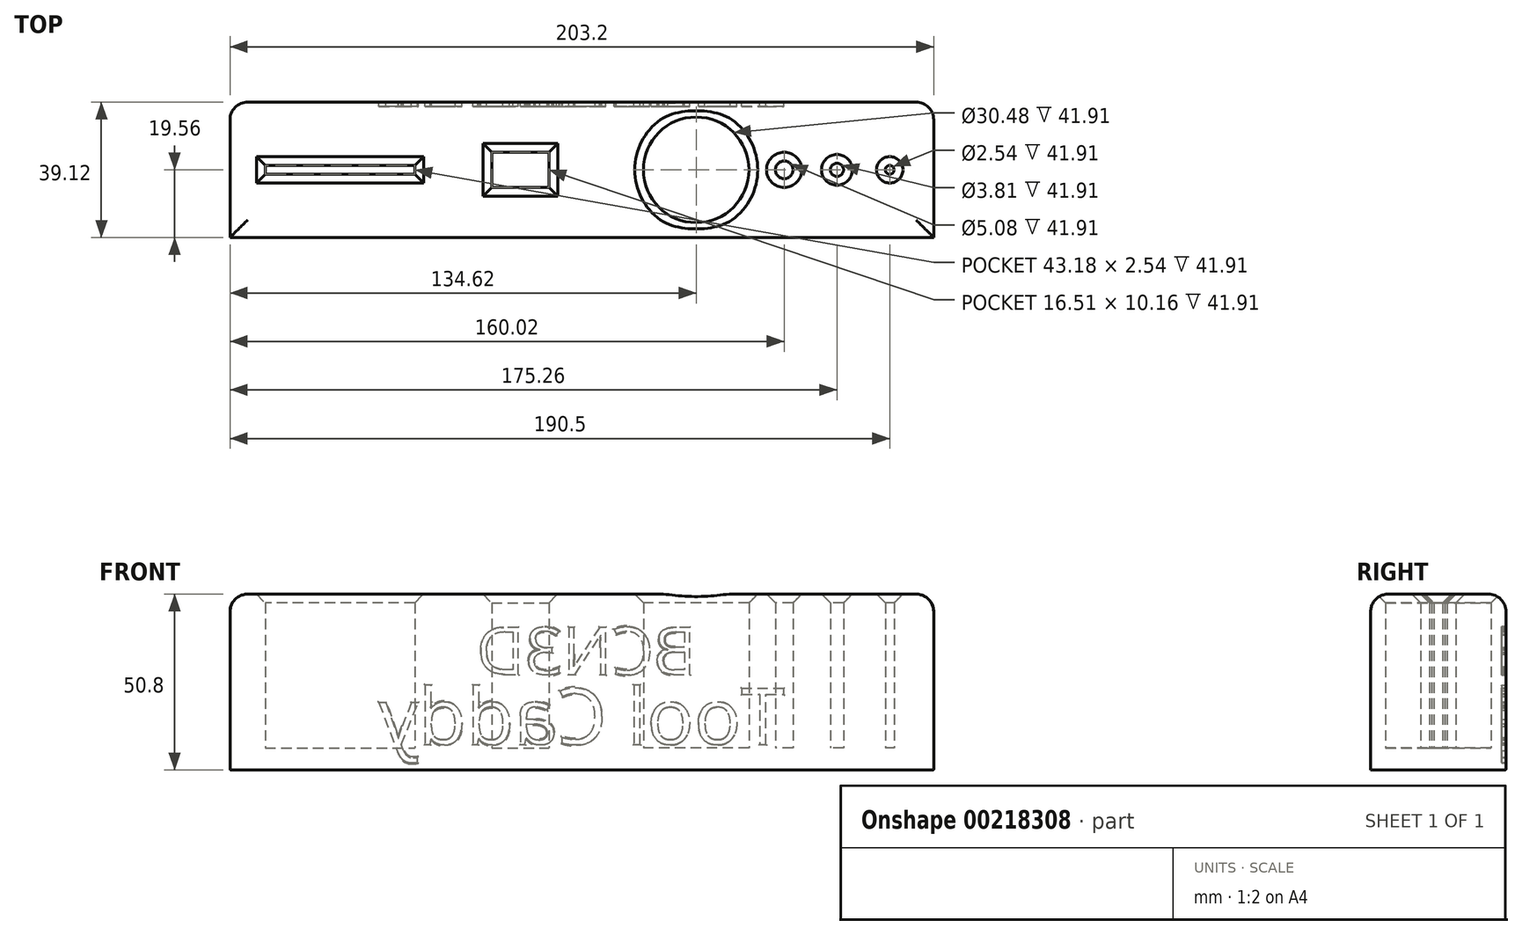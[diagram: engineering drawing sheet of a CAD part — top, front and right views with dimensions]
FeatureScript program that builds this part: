
annotation { "Feature Type Name" : "Feature", "Feature Type Description" : "" }
export const myFeature = defineFeature(function(context is Context, id is Id, definition is map)
    precondition{}
    {
        {
            var Q0;
            Q0=qCreatedBy(makeId("Top.planeOp"),FACE);
            var sketch = newSketch(context, id + "F0", { "sketchPlane" : qUnion([Q0])});
            skLineSegment(sketch, "E0.bottom", {"start": v(101.6, 19.56) * mm, "end": v(-101.6, 19.56) * mm});
            skLineSegment(sketch, "E0.top", {"start": v(101.6, -19.56) * mm, "end": v(-101.6, -19.56) * mm});
            skLineSegment(sketch, "E0.left", {"start": v(101.6, 19.56) * mm, "end": v(101.6, -19.56) * mm});
            skLineSegment(sketch, "E0.right", {"start": v(-101.6, 19.56) * mm, "end": v(-101.6, -19.56) * mm});
            skPoint(sketch, "E0.middle", {"position": v(0, 0) * mm});
            skLineSegment(sketch, "E1.bottom", {"start": v(-91.44, 1.27) * mm, "end": v(-48.26, 1.27) * mm});
            skLineSegment(sketch, "E1.top", {"start": v(-91.44, -1.27) * mm, "end": v(-48.26, -1.27) * mm});
            skLineSegment(sketch, "E1.left", {"start": v(-91.44, 1.27) * mm, "end": v(-91.44, -1.27) * mm});
            skLineSegment(sketch, "E1.right", {"start": v(-48.26, 1.27) * mm, "end": v(-48.26, -1.27) * mm});
            skPoint(sketch, "E1.middle", {"position": v(-69.85, 0) * mm});
            skLineSegment(sketch, "E2.bottom", {"start": v(-26.04, -5.08) * mm, "end": v(-9.53, -5.08) * mm});
            skLineSegment(sketch, "E2.top", {"start": v(-26.04, 5.08) * mm, "end": v(-9.53, 5.08) * mm});
            skLineSegment(sketch, "E2.left", {"start": v(-26.04, -5.08) * mm, "end": v(-26.04, 5.08) * mm});
            skLineSegment(sketch, "E2.right", {"start": v(-9.53, -5.08) * mm, "end": v(-9.53, 5.08) * mm});
            skPoint(sketch, "E2.middle", {"position": v(-17.78, 0) * mm});
            skCircle(sketch, "E3", {"center": v(58.42, 0) * mm, "radius": 2.54 * mm});
            skCircle(sketch, "E4", {"center": v(73.66, 0) * mm, "radius": 1.9 * mm});
            skCircle(sketch, "E5", {"center": v(88.9, 0) * mm, "radius": 1.27 * mm});
            skCircle(sketch, "E6", {"center": v(33.02, 0) * mm, "radius": 15.24 * mm});
            skSolve(sketch);
        }
        {
            var Q0;
            Q0=qSketchRegion(id+"F0",true);
            extrude(context, id + "F1", {"entities" : qUnion([Q0]), "depth" : 50.8 * mm});
        }
        {
            var Q0;
            Q0=makeQuery(id+"F0.imprint","IMPRINT",FACE,{"disambiguationData":[TD([[makeQuery(id+"F0.imprint","IMPRINT",EDGE,{"derivedFrom":sQuery(id+"F0.wireOp",EDGE,"E1.bottom")}),-1.0]])]});
            var Q1;
            Q1=makeQuery(id+"F0.imprint","IMPRINT",FACE,{"disambiguationData":[TD([[makeQuery(id+"F0.imprint","IMPRINT",EDGE,{"derivedFrom":sQuery(id+"F0.wireOp",EDGE,"E2.bottom")}),1.0]])]});
            var Q2;
            Q2=makeQuery(id+"F0.imprint","IMPRINT",FACE,{"disambiguationData":[TD([[makeQuery(id+"F0.imprint","IMPRINT",EDGE,{"derivedFrom":sQuery(id+"F0.wireOp",EDGE,"E3")}),1.0]])]});
            var Q3;
            Q3=makeQuery(id+"F0.imprint","IMPRINT",FACE,{"disambiguationData":[TD([[makeQuery(id+"F0.imprint","IMPRINT",EDGE,{"derivedFrom":sQuery(id+"F0.wireOp",EDGE,"E4")}),1.0]])]});
            var Q4;
            Q4=makeQuery(id+"F0.imprint","IMPRINT",FACE,{"disambiguationData":[TD([[makeQuery(id+"F0.imprint","IMPRINT",EDGE,{"derivedFrom":sQuery(id+"F0.wireOp",EDGE,"E5")}),1.0]])]});
            var Q5;
            Q5=makeQuery(id+"F0.imprint","IMPRINT",FACE,{"disambiguationData":[TD([[makeQuery(id+"F0.imprint","IMPRINT",EDGE,{"derivedFrom":sQuery(id+"F0.wireOp",EDGE,"E6")}),1.0]])]});
            extrude(context, id + "F2", {"entities" : qUnion([Q0, Q1, Q2, Q3, Q4, Q5]), "operationType" : NewBodyOperationType.ADD, "depth" : 6.35 * mm});
        }
        {
            var Q0;
            Q0=makeQuery(id+"F1.opExtrude","CAP_EDGE",EDGE,{"disambiguationData":[OSD([sQuery(id+"F0.wireOp",EDGE,"E1.bottom")])],"isStart":false});
            var Q1;
            Q1=makeQuery(id+"F1.opExtrude","CAP_EDGE",EDGE,{"disambiguationData":[OSD([sQuery(id+"F0.wireOp",EDGE,"E1.top")])],"isStart":false});
            var Q2;
            Q2=makeQuery(id+"F1.opExtrude","CAP_EDGE",EDGE,{"disambiguationData":[OSD([sQuery(id+"F0.wireOp",EDGE,"E1.left")])],"isStart":false});
            var Q3;
            Q3=makeQuery(id+"F1.opExtrude","CAP_EDGE",EDGE,{"disambiguationData":[OSD([sQuery(id+"F0.wireOp",EDGE,"E1.right")])],"isStart":false});
            var Q4;
            Q4=makeQuery(id+"F1.opExtrude","CAP_EDGE",EDGE,{"disambiguationData":[OSD([sQuery(id+"F0.wireOp",EDGE,"E2.bottom")])],"isStart":false});
            var Q5;
            Q5=makeQuery(id+"F1.opExtrude","CAP_EDGE",EDGE,{"disambiguationData":[OSD([sQuery(id+"F0.wireOp",EDGE,"E2.left")])],"isStart":false});
            var Q6;
            Q6=makeQuery(id+"F1.opExtrude","CAP_EDGE",EDGE,{"disambiguationData":[OSD([sQuery(id+"F0.wireOp",EDGE,"E2.top")])],"isStart":false});
            var Q7;
            Q7=makeQuery(id+"F1.opExtrude","CAP_EDGE",EDGE,{"disambiguationData":[OSD([sQuery(id+"F0.wireOp",EDGE,"E2.right")])],"isStart":false});
            var Q8;
            Q8=makeQuery(id+"F1.opExtrude","CAP_EDGE",EDGE,{"disambiguationData":[OSD([sQuery(id+"F0.wireOp",EDGE,"E3")])],"isStart":false});
            var Q9;
            Q9=makeQuery(id+"F1.opExtrude","CAP_EDGE",EDGE,{"disambiguationData":[OSD([sQuery(id+"F0.wireOp",EDGE,"E4")])],"isStart":false});
            var Q10;
            Q10=makeQuery(id+"F1.opExtrude","CAP_EDGE",EDGE,{"disambiguationData":[OSD([sQuery(id+"F0.wireOp",EDGE,"E5")])],"isStart":false});
            var Q11;
            Q11=makeQuery(id+"F1.opExtrude","CAP_EDGE",EDGE,{"disambiguationData":[OSD([sQuery(id+"F0.wireOp",EDGE,"E6")])],"isStart":false});
            chamfer(context, id + "F3", {"entities" : qUnion([Q0, Q1, Q2, Q3, Q4, Q5, Q6, Q7, Q8, Q9, Q10, Q11]), "width" : 2.54 * mm, "tangentPropagation" : true});
        }
        {
            var Q0;
            Q0=makeQuery(id+"F1.opExtrude","CAP_EDGE",EDGE,{"disambiguationData":[OSD([sQuery(id+"F0.wireOp",EDGE,"E0.right")])],"isStart":false});
            var Q1;
            Q1=makeQuery(id+"F1.opExtrude","CAP_EDGE",EDGE,{"disambiguationData":[OSD([sQuery(id+"F0.wireOp",EDGE,"E0.top")])],"isStart":false});
            var Q2;
            Q2=makeQuery(id+"F1.opExtrude","CAP_EDGE",EDGE,{"disambiguationData":[OSD([sQuery(id+"F0.wireOp",EDGE,"E0.bottom")])],"isStart":false});
            var Q3;
            Q3=makeQuery(id+"F1.opExtrude","CAP_EDGE",EDGE,{"disambiguationData":[OSD([sQuery(id+"F0.wireOp",EDGE,"E0.left")])],"isStart":false});
            var Q4;
            Q4=makeQuery(id+"F1.opExtrude","SWEPT_EDGE",EDGE,{"disambiguationData":[OSD([sQuery(id+"F0.wireOp",EDGE,"E0.bottom"),sQuery(id+"F0.wireOp",EDGE,"E0.right")])]});
            var Q5;
            Q5=makeQuery(id+"F1.opExtrude","SWEPT_EDGE",EDGE,{"disambiguationData":[OSD([sQuery(id+"F0.wireOp",EDGE,"E0.bottom"),sQuery(id+"F0.wireOp",EDGE,"E0.left")])]});
            fillet(context, id + "F4", {"entities" : qUnion([Q0, Q1, Q2, Q3, Q4, Q5]), "radius" : 5.08 * mm, "tangentPropagation" : true, "allowEdgeOverflow" : false});
        }
        {
            var Q0;
            Q0=makeQuery(id+"F1.opExtrude","SWEPT_FACE",FACE,{"disambiguationData":[OSD([sQuery(id+"F0.wireOp",EDGE,"E0.bottom")])]});
            var sketch = newSketch(context, id + "F5", { "sketchPlane" : qUnion([Q0])});
            skText(sketch, "E7", { "text": "Tool Caddy", "fontName": "OpenSans-Regular.ttf"});
            skText(sketch, "E8", { "text": "BCN3D", "fontName": "OpenSans-Regular.ttf"});
            const initialGuessF5  = {"E7": [-0.05847, 0.00741, 1, 0, 0.01624], "E8": [-0.03305, 0.02761, 1, 0, 0.0137]};
            skSetInitialGuess(sketch, initialGuessF5);
            skSolve(sketch);
        }
        {
            var Q0;
            Q0=qSketchRegion(id+"F5",true);
            extrude(context, id + "F6", {"entities" : qUnion([Q0]), "operationType" : NewBodyOperationType.REMOVE, "oppositeDirection" : true, "depth" : 1.27 * mm});
        }
        {
            var Q0;
            {var subQ2=sQuery(id+"F0.wireOp",EDGE,"E3");var subQ13=sQuery(id+"F0.wireOp",EDGE,"E0.bottom");Q0=makeQuery(id+"F6.boolean.opBoolean","SPLIT",FACE,{"disambiguationData":[TD([makeQuery(id+"F2.opExtrude","CAP_FACE",FACE,{"disambiguationData":[OSD([subQ2])],"isStart":true})])],"derivedFrom":makeQuery(id+"F1.opExtrude","SWEPT_FACE",FACE,{"disambiguationData":[OSD([subQ13])]})});}
            var Q1;
            Q1=makeQuery(id+"F6.boolean.opBoolean","SPLIT",FACE,{"disambiguationData":[TD([makeQuery(id+"F6.opExtrude","SWEPT_FACE",FACE,{"disambiguationData":[OSD([sQuery(id+"F5.wireOp",EDGE,"E8.sketch_text.stroke-11")])]})])],"derivedFrom":makeQuery(id+"F1.opExtrude","SWEPT_FACE",FACE,{"disambiguationData":[OSD([sQuery(id+"F0.wireOp",EDGE,"E0.bottom")])]})});
            var Q2;
            Q2=makeQuery(id+"F6.boolean.opBoolean","SPLIT",FACE,{"disambiguationData":[TD([makeQuery(id+"F6.opExtrude","SWEPT_FACE",FACE,{"disambiguationData":[OSD([sQuery(id+"F5.wireOp",EDGE,"E8.sketch_text.stroke-18")])]})])],"derivedFrom":makeQuery(id+"F1.opExtrude","SWEPT_FACE",FACE,{"disambiguationData":[OSD([sQuery(id+"F0.wireOp",EDGE,"E0.bottom")])]})});
            var Q3;
            Q3=makeQuery(id+"F6.boolean.opBoolean","SPLIT",FACE,{"disambiguationData":[TD([makeQuery(id+"F6.opExtrude","SWEPT_FACE",FACE,{"disambiguationData":[OSD([sQuery(id+"F5.wireOp",EDGE,"E8.sketch_text.stroke-90")])]})])],"derivedFrom":makeQuery(id+"F1.opExtrude","SWEPT_FACE",FACE,{"disambiguationData":[OSD([sQuery(id+"F0.wireOp",EDGE,"E0.bottom")])]})});
            var Q4;
            Q4=makeQuery(id+"F6.boolean.opBoolean","SPLIT",FACE,{"disambiguationData":[TD([makeQuery(id+"F6.opExtrude","SWEPT_FACE",FACE,{"disambiguationData":[OSD([sQuery(id+"F5.wireOp",EDGE,"E7.sketch_text.stroke-127")])]})])],"derivedFrom":makeQuery(id+"F1.opExtrude","SWEPT_FACE",FACE,{"disambiguationData":[OSD([sQuery(id+"F0.wireOp",EDGE,"E0.bottom")])]})});
            var Q5;
            Q5=makeQuery(id+"F6.boolean.opBoolean","SPLIT",FACE,{"disambiguationData":[TD([makeQuery(id+"F6.opExtrude","SWEPT_FACE",FACE,{"disambiguationData":[OSD([sQuery(id+"F5.wireOp",EDGE,"E7.sketch_text.stroke-103")])]})])],"derivedFrom":makeQuery(id+"F1.opExtrude","SWEPT_FACE",FACE,{"disambiguationData":[OSD([sQuery(id+"F0.wireOp",EDGE,"E0.bottom")])]})});
            var Q6;
            Q6=makeQuery(id+"F6.boolean.opBoolean","SPLIT",FACE,{"disambiguationData":[TD([makeQuery(id+"F6.opExtrude","SWEPT_FACE",FACE,{"disambiguationData":[OSD([sQuery(id+"F5.wireOp",EDGE,"E7.sketch_text.stroke-80")])]})])],"derivedFrom":makeQuery(id+"F1.opExtrude","SWEPT_FACE",FACE,{"disambiguationData":[OSD([sQuery(id+"F0.wireOp",EDGE,"E0.bottom")])]})});
            var Q7;
            Q7=makeQuery(id+"F6.boolean.opBoolean","SPLIT",FACE,{"disambiguationData":[TD([makeQuery(id+"F6.opExtrude","SWEPT_FACE",FACE,{"disambiguationData":[OSD([sQuery(id+"F5.wireOp",EDGE,"E7.sketch_text.stroke-34")])]})])],"derivedFrom":makeQuery(id+"F1.opExtrude","SWEPT_FACE",FACE,{"disambiguationData":[OSD([sQuery(id+"F0.wireOp",EDGE,"E0.bottom")])]})});
            var Q8;
            Q8=makeQuery(id+"F6.boolean.opBoolean","SPLIT",FACE,{"disambiguationData":[TD([makeQuery(id+"F6.opExtrude","SWEPT_FACE",FACE,{"disambiguationData":[OSD([sQuery(id+"F5.wireOp",EDGE,"E7.sketch_text.stroke-17")])]})])],"derivedFrom":makeQuery(id+"F1.opExtrude","SWEPT_FACE",FACE,{"disambiguationData":[OSD([sQuery(id+"F0.wireOp",EDGE,"E0.bottom")])]})});
            fillet(context, id + "F7", {"entities" : qUnion([Q0, Q1, Q2, Q3, Q4, Q5, Q6, Q7, Q8]), "radius" : 0.25 * mm, "tangentPropagation" : true, "allowEdgeOverflow" : false});
        }
    });
